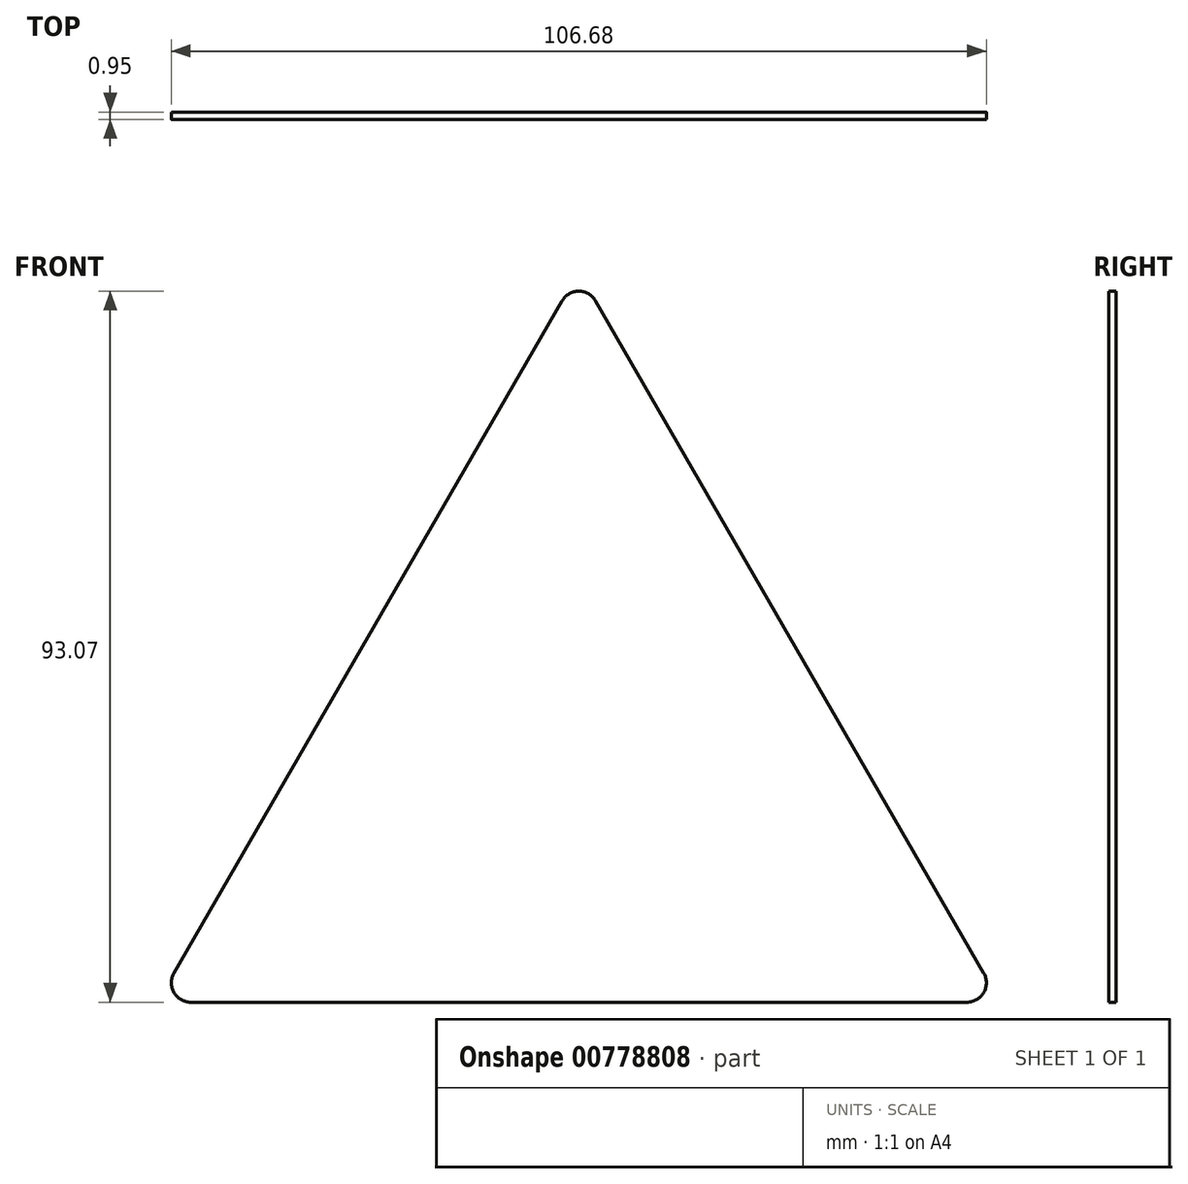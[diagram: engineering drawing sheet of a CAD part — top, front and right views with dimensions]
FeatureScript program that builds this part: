
annotation { "Feature Type Name" : "Feature", "Feature Type Description" : "" }
export const myFeature = defineFeature(function(context is Context, id is Id, definition is map)
    precondition{}
    {
        {
            var Q0;
            Q0=qCreatedBy(makeId("Front.planeOp"),FACE);
            var sketch = newSketch(context, id + "F0", { "sketchPlane" : qUnion([Q0])});
            skLineSegment(sketch, "E0", {"start": v(-50.8, 0) * mm, "end": v(50.8, 0) * mm});
            skLineSegment(sketch, "E1", {"start": v(53, 3.81) * mm, "end": v(2.2, 91.8) * mm});
            skLineSegment(sketch, "E2", {"start": v(-2.2, 91.8) * mm, "end": v(-53, 3.8) * mm});
            skArc(sketch, "E3", {"start": v(2.2, 91.8) * mm, "mid": v(0, 93.07) * mm, "end": v(-2.2, 91.8) * mm});
            skArc(sketch, "E4", {"start": v(50.8, 0) * mm, "mid": v(53, 1.27) * mm, "end": v(53, 3.81) * mm});
            skArc(sketch, "E5", {"start": v(-53, 3.8) * mm, "mid": v(-53, 1.27) * mm, "end": v(-50.8, 0) * mm});
            skPoint(sketch, "E6.orphan", {"position": v(0, 95.6) * mm});
            skPoint(sketch, "E7.orphan", {"position": v(-55.2, 0) * mm});
            skSolve(sketch);
        }
        {
            var Q0;
            Q0 = qSketchRegion(id + "F0", true);
            extrude(context, id + "F1", {"entities" : qUnion([Q0]), "depth" : 0.95 * mm, "offsetDistance" : 25.4 * mm});
        }
    });
